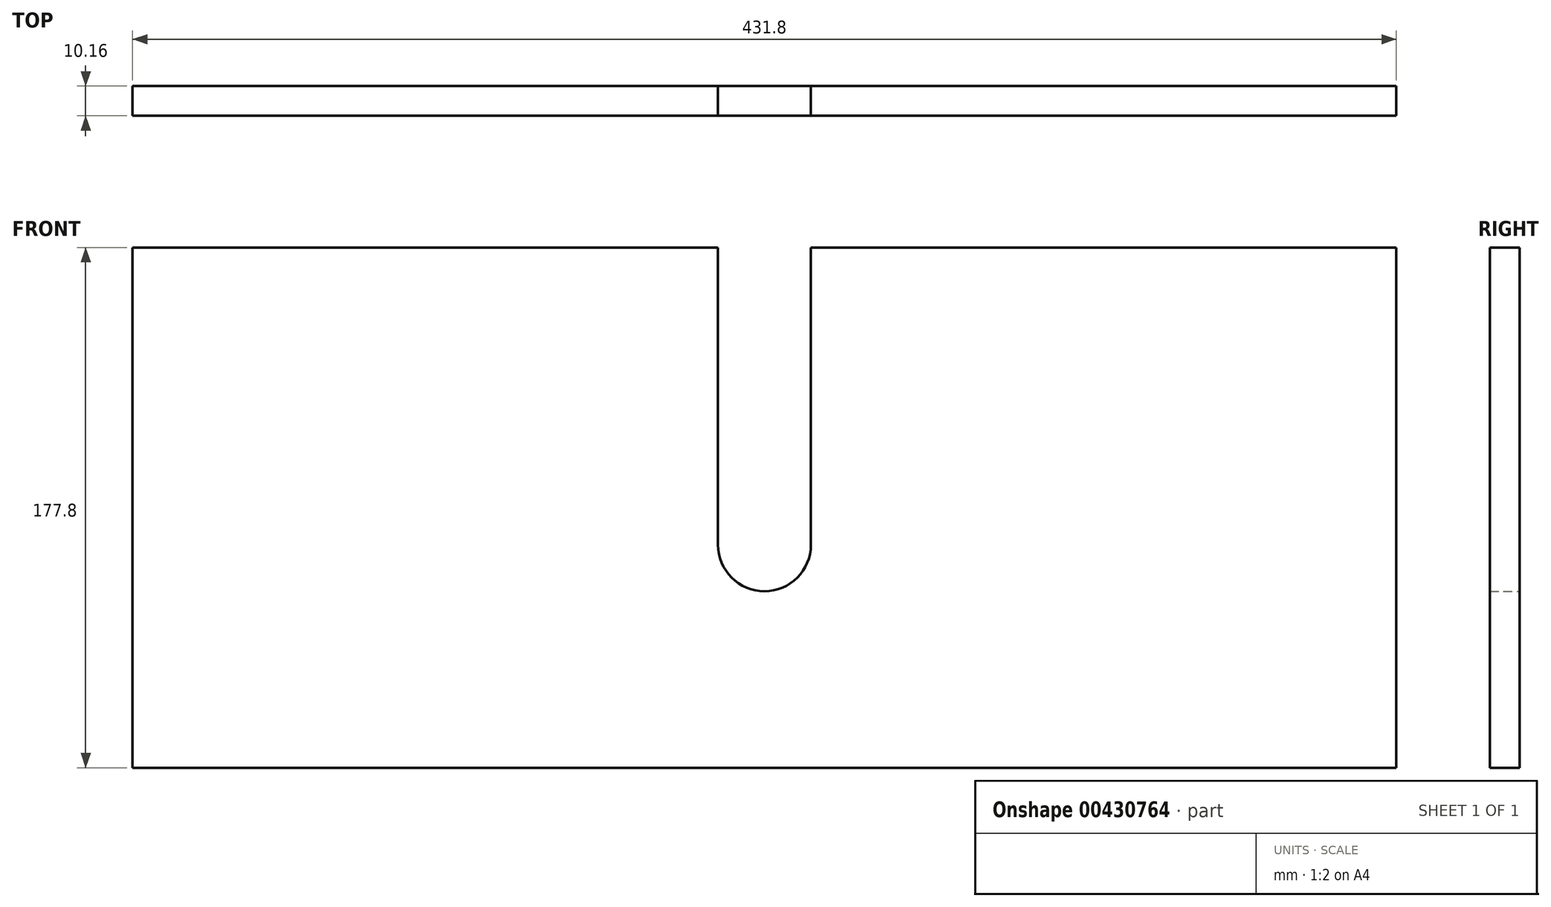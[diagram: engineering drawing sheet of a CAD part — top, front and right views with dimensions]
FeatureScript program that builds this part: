
annotation { "Feature Type Name" : "Feature", "Feature Type Description" : "" }
export const myFeature = defineFeature(function(context is Context, id is Id, definition is map)
    precondition{}
    {
        {
            var Q0;
            Q0=qCreatedBy(makeId("Front.planeOp"),FACE);
            var sketch = newSketch(context, id + "F0", { "sketchPlane" : qUnion([Q0])});
            skLineSegment(sketch, "E0.bottom", {"start": v(0, 0) * mm, "end": v(215.9, 0) * mm});
            skLineSegment(sketch, "E0.top", {"start": v(0, 177.8) * mm, "end": v(215.9, 177.8) * mm});
            skLineSegment(sketch, "E0.left", {"start": v(0, 0) * mm, "end": v(0, 177.8) * mm});
            skLineSegment(sketch, "E0.right", {"start": v(215.9, 0) * mm, "end": v(215.9, 177.8) * mm});
            skLineSegment(sketch, "E1.bottom", {"start": v(0, 177.8) * mm, "end": v(15.87, 177.8) * mm});
            skLineSegment(sketch, "E1.top", {"start": v(0, 76.2) * mm, "end": v(15.87, 76.2) * mm});
            skLineSegment(sketch, "E1.left", {"start": v(0, 177.8) * mm, "end": v(0, 76.2) * mm});
            skLineSegment(sketch, "E1.right", {"start": v(15.87, 177.8) * mm, "end": v(15.87, 76.2) * mm});
            skArc(sketch, "E2", {"start": v(0, 60.33) * mm, "mid": v(11.23, 64.97) * mm, "end": v(15.87, 76.2) * mm});
            skSolve(sketch);
        }
        {
            var Q0;
            {var subQ1=sQuery(id+"F0.wireOp",EDGE,"E0.bottom");Q0=makeQuery(id+"F0.imprint","IMPRINT",FACE,{"disambiguationData":[TD([[makeQuery(id+"F0.imprint","IMPRINT",EDGE,{"derivedFrom":subQ1}),1.0]])]});}
            extrude(context, id + "F1", {"entities" : qUnion([Q0]), "depth" : 10.16 * mm});
        }
        {
            var Q0;
            Q0=makeQuery(id+"F1.opExtrude","SWEPT_BODY",BODY,{"disambiguationData":[OSD([sQuery(id+"F0.wireOp",EDGE,"E0.bottom"),sQuery(id+"F0.wireOp",EDGE,"E0.top"),sQuery(id+"F0.wireOp",EDGE,"E0.left"),sQuery(id+"F0.wireOp",EDGE,"E0.right"),sQuery(id+"F0.wireOp",EDGE,"E1.right"),sQuery(id+"F0.wireOp",EDGE,"E2")])]});
            var Q1;
            Q1=qCreatedBy(makeId("Right.planeOp"),FACE);
            mirror(context, id + "F2", {"operationType" : NewBodyOperationType.ADD, "entities" : qUnion([Q0]), "mirrorPlane" : qUnion([Q1])});
        }
    });
